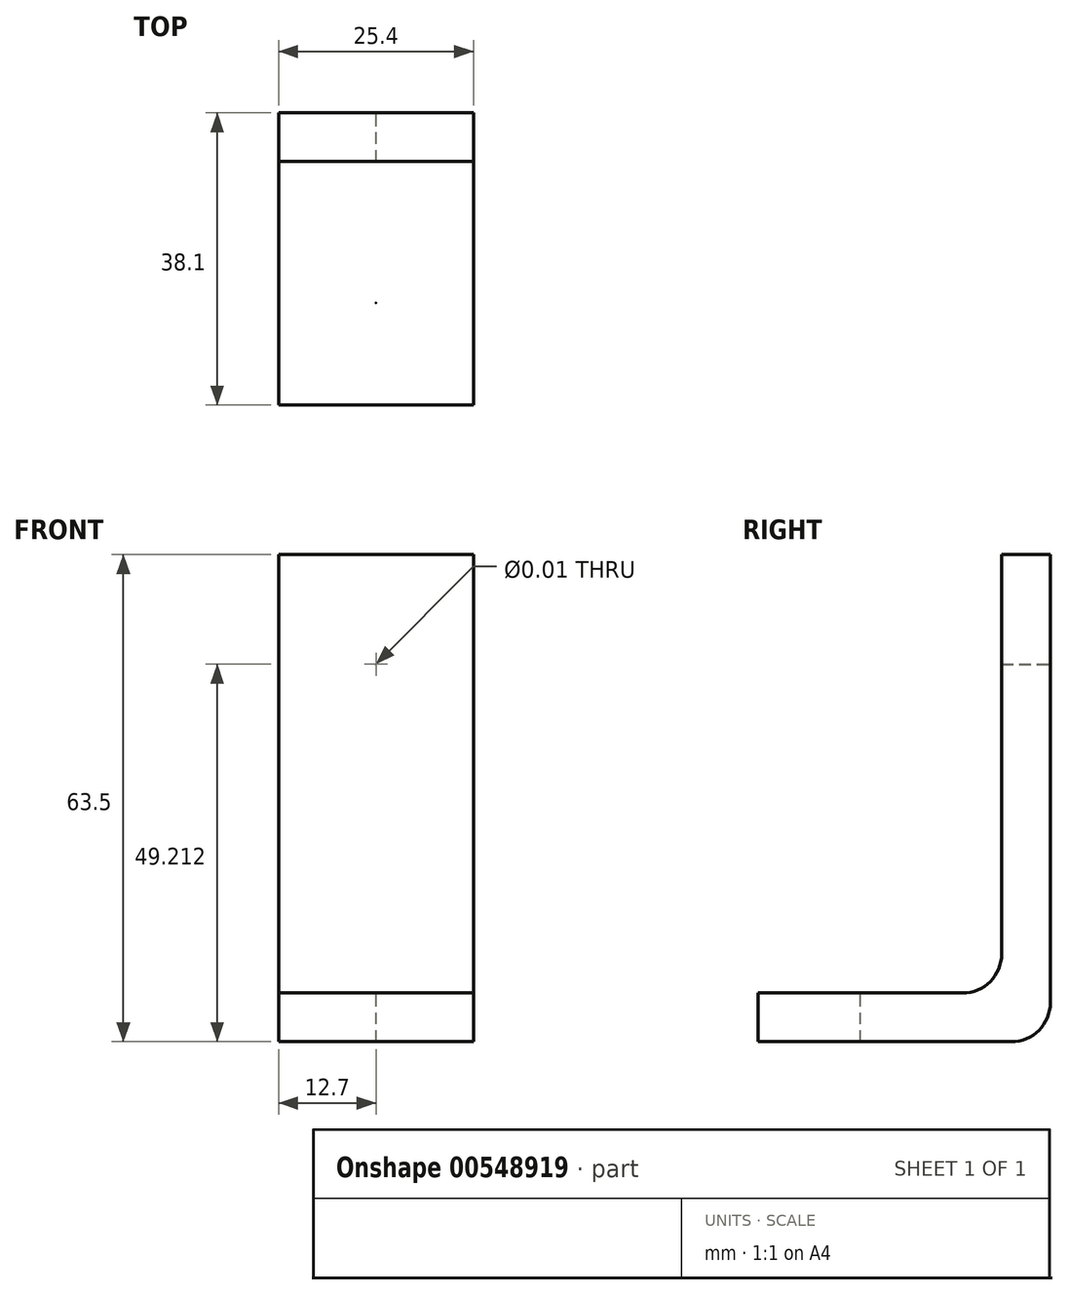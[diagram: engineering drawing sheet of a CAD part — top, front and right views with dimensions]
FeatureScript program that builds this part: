
annotation { "Feature Type Name" : "Feature", "Feature Type Description" : "" }
export const myFeature = defineFeature(function(context is Context, id is Id, definition is map)
    precondition{}
    {
        {
            var Q0;
            Q0=qCreatedBy(makeId("Front.planeOp"),FACE);
            var sketch = newSketch(context, id + "F0", { "sketchPlane" : qUnion([Q0])});
            skLineSegment(sketch, "E0.bottom", {"start": v(0, 0) * mm, "end": v(25.4, 0) * mm});
            skLineSegment(sketch, "E0.top", {"start": v(0, 63.5) * mm, "end": v(25.4, 63.5) * mm});
            skLineSegment(sketch, "E0.left", {"start": v(0, 0) * mm, "end": v(0, 63.5) * mm});
            skLineSegment(sketch, "E0.right", {"start": v(25.4, 0) * mm, "end": v(25.4, 63.5) * mm});
            skLineSegment(sketch, "E1.top", {"start": v(0, 6.35) * mm, "end": v(25.4, 6.35) * mm});
            skLineSegment(sketch, "E1.left", {"start": v(0, 0) * mm, "end": v(0, 6.35) * mm});
            skLineSegment(sketch, "E1.right", {"start": v(25.4, 0) * mm, "end": v(25.4, 6.35) * mm});
            skLineSegment(sketch, "E2", {"start": v(12.7, 0) * mm, "end": v(12.7, 63.5) * mm});
            skPoint(sketch, "E3", {"position": v(12.7, 49.21) * mm});
            skSolve(sketch);
        }
        {
            var Q0;
            Q0=makeQuery(id+"F0.imprint","IMPRINT",FACE,{"disambiguationData":[TD([[makeQuery(id+"F0.imprint","IMPRINT",EDGE,{"derivedFrom":sQuery(id+"F0.wireOp",EDGE,"E0.bottom")}),1.0]])]});
            extrude(context, id + "F1", {"entities" : qUnion([Q0]), "depth" : 38.1 * mm, "offsetDistance" : 25.4 * mm});
        }
        {
            var Q0;
            Q0 = qSketchRegion(id + "F0", true);
            extrude(context, id + "F2", {"entities" : qUnion([Q0]), "operationType" : NewBodyOperationType.ADD, "depth" : 6.35 * mm, "offsetDistance" : 25.4 * mm});
        }
        {
            var Q0;
            Q0=makeQuery(id+"F2.boolean.opBoolean","INTERSECT",EDGE,{"derivedFrom":[makeQuery(id+"F1.opExtrude","SWEPT_FACE",FACE,{"disambiguationData":[OSD([sQuery(id+"F0.wireOp",EDGE,"E1.top")])]}),makeQuery(id+"F2.opExtrude","CAP_FACE",FACE,{"disambiguationData":[OSD([sQuery(id+"F0.wireOp",EDGE,"E0.top"),sQuery(id+"F0.wireOp",EDGE,"E0.left"),sQuery(id+"F0.wireOp",EDGE,"E0.right"),sQuery(id+"F0.wireOp",EDGE,"E0.bottom"),sQuery(id+"F0.wireOp",EDGE,"E1.left"),sQuery(id+"F0.wireOp",EDGE,"E1.right")])],"isStart":false})]});
            var Q1;
            Q1=makeQuery(id+"F1.opExtrude","CAP_EDGE",EDGE,{"disambiguationData":[OSD([sQuery(id+"F0.wireOp",EDGE,"E0.bottom")])],"isStart":true});
            fillet(context, id + "F3", {"entities" : qUnion([Q0, Q1]), "radius" : 5.08 * mm, "tangentPropagation" : true, "allowEdgeOverflow" : false});
        }
        {
            var Q0;
            Q0=makeQuery(id+"F1.opExtrude","SWEPT_FACE",FACE,{"disambiguationData":[OSD([sQuery(id+"F0.wireOp",EDGE,"E1.top")])]});
            var sketch = newSketch(context, id + "F4", { "sketchPlane" : qUnion([Q0])});
            skLineSegment(sketch, "E4", {"start": v(0, -11.43) * mm, "end": v(25.4, -38.1) * mm});
            skPoint(sketch, "E5", {"position": v(12.7, -24.77) * mm});
            skSolve(sketch);
        }
        {
            var Q0;
            Q0=sQuery(id+"F4.wireOp",VERTEX,"E5");
            var Q1;
            Q1=makeQuery(id+"F1.opExtrude","SWEPT_BODY",BODY,{"disambiguationData":[OSD([sQuery(id+"F0.wireOp",EDGE,"E0.bottom"),sQuery(id+"F0.wireOp",EDGE,"E1.top"),sQuery(id+"F0.wireOp",EDGE,"E1.left"),sQuery(id+"F0.wireOp",EDGE,"E1.right")])]});
            hole(context, id + "F5", {"style" : HoleStyle.SIMPLE, "endStyle" : HoleEndStyle.THROUGH, "standardTappedOrClearance" : lookupTablePath({ "standard" : "ANSI", "size" : "3/8 (0.38)", "type" : "Drilled" }), "standardBlindInLast" : lookupTablePath({ "standard" : "ANSI", "size" : "3/8", "type" : "Drilled" }), "holeDiameter" : 3 / 203.2 * mm, "isTappedThrough" : true, "tappedDepth" : 12.7 * mm, "tapClearance" : 3, "locations" : qUnion([Q0]), "scope" : qUnion([Q1])});
        }
        {
            var Q0;
            Q0=sQuery(id+"F0.wireOp",VERTEX,"E3");
            var Q1;
            Q1=makeQuery(id+"F1.opExtrude","SWEPT_BODY",BODY,{"disambiguationData":[OSD([sQuery(id+"F0.wireOp",EDGE,"E0.bottom"),sQuery(id+"F0.wireOp",EDGE,"E1.top"),sQuery(id+"F0.wireOp",EDGE,"E1.left"),sQuery(id+"F0.wireOp",EDGE,"E1.right")])]});
            hole(context, id + "F6", {"style" : HoleStyle.SIMPLE, "endStyle" : HoleEndStyle.THROUGH, "oppositeDirection" : true, "standardTappedOrClearance" : lookupTablePath({ "standard" : "ANSI", "size" : "3/8 (0.38)", "type" : "Drilled" }), "standardBlindInLast" : lookupTablePath({ "standard" : "ANSI", "size" : "3/8", "type" : "Drilled" }), "holeDiameter" : 3 / 203.2 * mm, "isTappedThrough" : true, "tappedDepth" : 12.7 * mm, "tapClearance" : 3, "locations" : qUnion([Q0]), "scope" : qUnion([Q1])});
        }
    });
